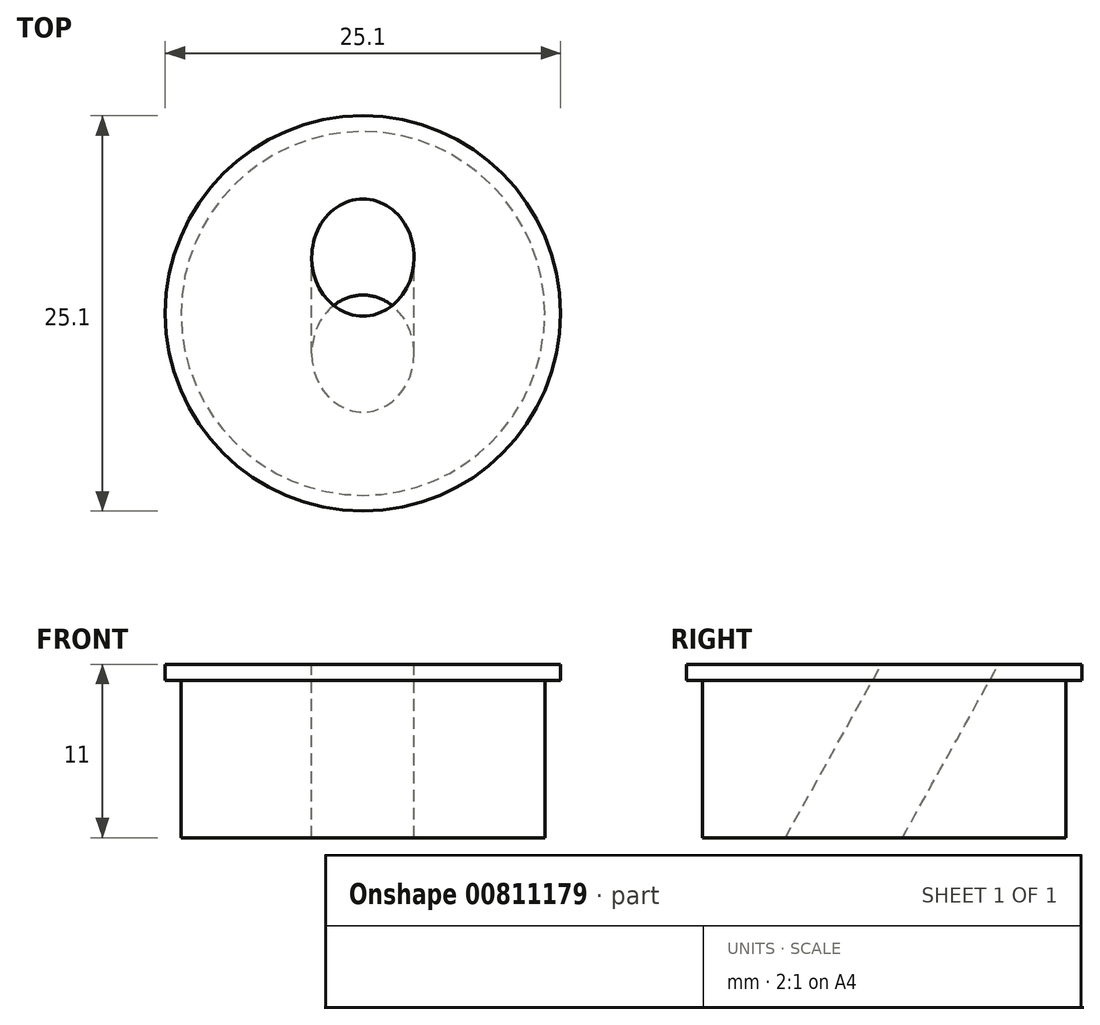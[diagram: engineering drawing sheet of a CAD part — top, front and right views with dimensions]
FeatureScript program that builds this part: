
annotation { "Feature Type Name" : "Feature", "Feature Type Description" : "" }
export const myFeature = defineFeature(function(context is Context, id is Id, definition is map)
    precondition{}
    {
        {
            var Q0;
            Q0=qCreatedBy(makeId("Top.planeOp"),FACE);
            var sketch = newSketch(context, id + "F0", { "sketchPlane" : qUnion([Q0])});
            skCircle(sketch, "E0", {"center": v(0, 0) * mm, "radius": 11.55 * mm});
            skSolve(sketch);
        }
        {
            var Q0;
            Q0 = qSketchRegion(id + "F0", true);
            extrude(context, id + "F1", {"entities" : qUnion([Q0]), "depth" : 10 * mm, "offsetDistance" : 25 * mm});
        }
        {
            var Q0;
            Q0=makeQuery(id+"F1.opExtrude","CAP_FACE",FACE,{"disambiguationData":[OSD([sQuery(id+"F0.wireOp",EDGE,"E0")])],"isStart":false});
            var sketch = newSketch(context, id + "F2", { "sketchPlane" : qUnion([Q0])});
            skCircle(sketch, "E1", {"center": v(0, 0) * mm, "radius": 12.55 * mm});
            skCircle(sketch, "E2.0", {"center": v(0, 0) * mm, "radius": 11.55 * mm, "construction": true});
            skSolve(sketch);
        }
        {
            var Q0;
            Q0=makeQuery(id+"F2.imprint","IMPRINT",FACE,{"disambiguationData":[TD([[makeQuery(id+"F2.imprint","IMPRINT",EDGE,{"derivedFrom":sQuery(id+"F2.wireOp",EDGE,"E1")}),1.0]])]});
            var Q1;
            Q1=makeQuery(id+"F2.imprint","IMPRINT",FACE,{"disambiguationData":[TD([[makeQuery(id+"F2.imprint","IMPRINT",EDGE,{"derivedFrom":makeQuery(id+"F1.opExtrude","CAP_EDGE",EDGE,{"disambiguationData":[OSD([sQuery(id+"F0.wireOp",EDGE,"E0")])],"isStart":false})}),1.0]])]});
            extrude(context, id + "F3", {"entities" : qUnion([Q0, Q1]), "operationType" : NewBodyOperationType.ADD, "depth" : 1 * mm, "offsetDistance" : 25 * mm});
        }
        {
            var Q0;
            Q0=makeQuery(id+"F1.opExtrude","CAP_FACE",FACE,{"disambiguationData":[OSD([sQuery(id+"F0.wireOp",EDGE,"E0")])],"isStart":true});
            var sketch = newSketch(context, id + "F4", { "sketchPlane" : qUnion([Q0])});
            skPoint(sketch, "E3", {"position": v(0, 2.55) * mm});
            skSolve(sketch);
        }
        {
            var Q0;
            Q0=qCreatedBy(makeId("Right.planeOp"),FACE);
            var sketch = newSketch(context, id + "F5", { "sketchPlane" : qUnion([Q0])});
            skPoint(sketch, "E4.0", {"position": v(-2.55, 0) * mm});
            skPoint(sketch, "E5.0", {"position": v(3.55, 11) * mm});
            skLineSegment(sketch, "E6", {"start": v(-2.55, 0) * mm, "end": v(6.25, 15.86) * mm});
            skLineSegment(sketch, "E7.0", {"start": v(-12.55, 11) * mm, "end": v(12.55, 11) * mm, "construction": true});
            skSolve(sketch);
        }
        {
            var Q0;
            Q0=sQuery(id+"F5.wireOp",EDGE,"E6");
            var Q1;
            Q1=sQuery(id+"F5.wireOp",VERTEX,"E6.end");
            cPlane(context, id + "F6", {"entities" : qUnion([Q0, Q1]), "cplaneType" : CPlaneType.LINE_POINT, "offset" : 25 * mm, "width" : 150 * mm, "height" : 150 * mm});
        }
        {
            var Q0;
            Q0=qCreatedBy(id+"F6.planeOp",FACE);
            var sketch = newSketch(context, id + "F7", { "sketchPlane" : qUnion([Q0])});
            skPoint(sketch, "E8.0", {"position": v(0, -2.23) * mm});
            skCircle(sketch, "E9", {"center": v(0, -2.23) * mm, "radius": 3.25 * mm});
            skSolve(sketch);
        }
        {
            var Q0;
            Q0=makeQuery(id+"F7.imprint","IMPRINT",FACE,{"disambiguationData":[TD([[makeQuery(id+"F7.imprint","IMPRINT",EDGE,{"derivedFrom":sQuery(id+"F7.wireOp",EDGE,"E9")}),1.0]])]});
            var Q1;
            Q1=makeQuery(id+"F1.opExtrude","CAP_FACE",FACE,{"disambiguationData":[OSD([sQuery(id+"F0.wireOp",EDGE,"E0")])],"isStart":true});
            extrude(context, id + "F8", {"entities" : qUnion([Q0]), "operationType" : NewBodyOperationType.REMOVE, "oppositeDirection" : true, "depth" : 27.57 * mm, "endBoundEntityFace" : qUnion([Q1]), "offsetDistance" : 25 * mm});
        }
    });
